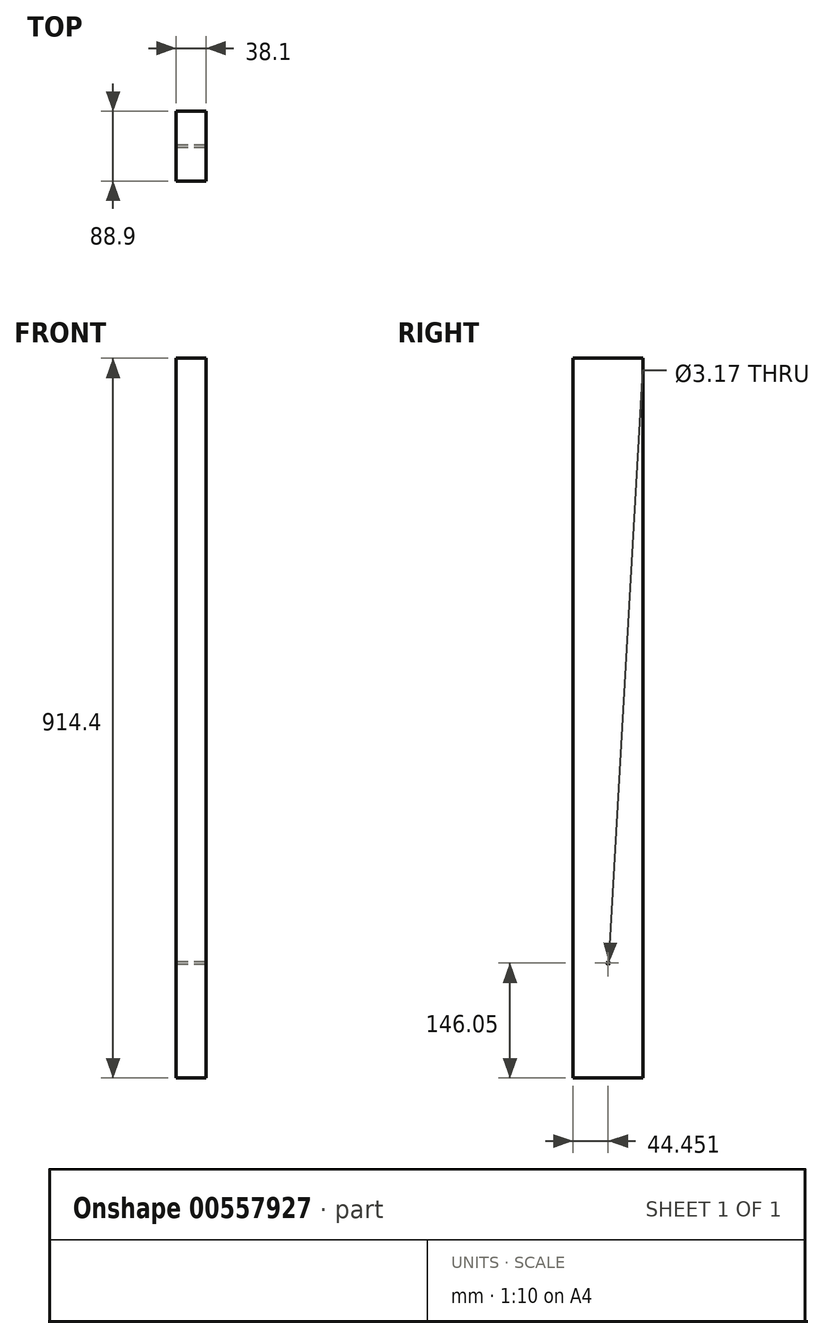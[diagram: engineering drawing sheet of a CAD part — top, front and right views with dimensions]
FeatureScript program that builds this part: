
annotation { "Feature Type Name" : "Feature", "Feature Type Description" : "" }
export const myFeature = defineFeature(function(context is Context, id is Id, definition is map)
    precondition{}
    {
        {
            var Q0;
            Q0=qCreatedBy(makeId("Right.planeOp"),FACE);
            var sketch = newSketch(context, id + "F0", { "sketchPlane" : qUnion([Q0])});
            skLineSegment(sketch, "E0.bottom", {"start": v(77.94, 35.56) * mm, "end": v(166.84, 35.56) * mm});
            skLineSegment(sketch, "E0.top", {"start": v(77.94, 949.96) * mm, "end": v(166.84, 949.96) * mm});
            skLineSegment(sketch, "E0.left", {"start": v(77.94, 35.56) * mm, "end": v(77.94, 949.96) * mm});
            skLineSegment(sketch, "E0.right", {"start": v(166.84, 35.56) * mm, "end": v(166.84, 949.96) * mm});
            skCircle(sketch, "E1", {"center": v(122.4, 181.61) * mm, "radius": 1.59 * mm});
            skSolve(sketch);
        }
        {
            var Q0;
            Q0=makeQuery(id+"F0.imprint","IMPRINT",FACE,{"disambiguationData":[TD([[makeQuery(id+"F0.imprint","IMPRINT",EDGE,{"derivedFrom":sQuery(id+"F0.wireOp",EDGE,"E0.bottom")}),1.0]])]});
            extrude(context, id + "F1", {"entities" : qUnion([Q0]), "depth" : 38.1 * mm, "offsetDistance" : 25.4 * mm});
        }
    });
